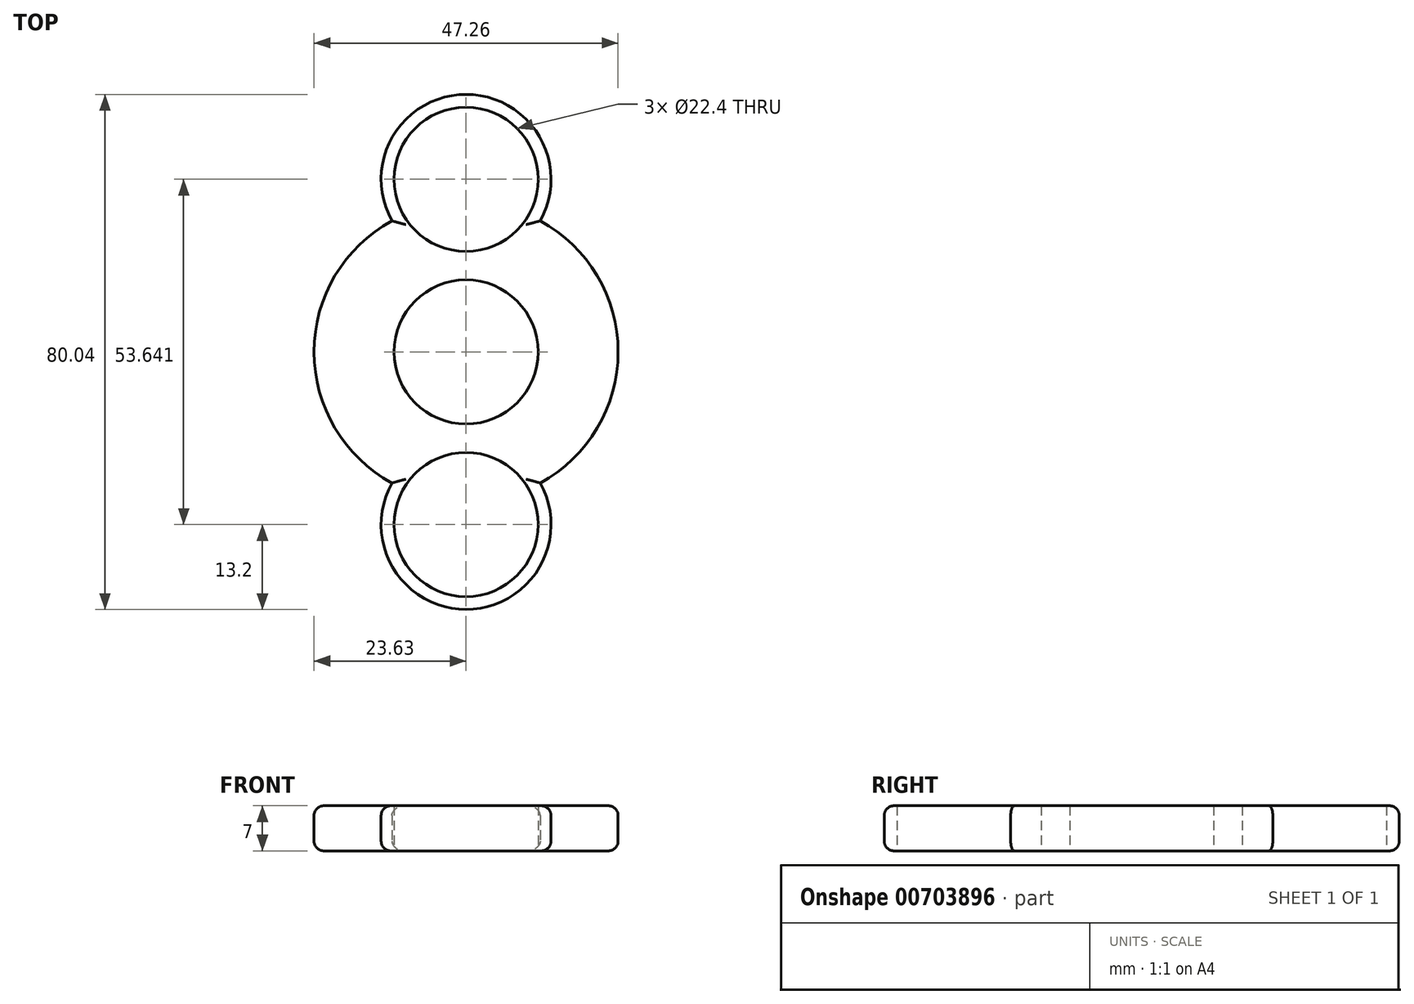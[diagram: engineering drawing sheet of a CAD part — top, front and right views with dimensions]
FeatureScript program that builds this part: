
annotation { "Feature Type Name" : "Feature", "Feature Type Description" : "" }
export const myFeature = defineFeature(function(context is Context, id is Id, definition is map)
    precondition{}
    {
        {
            var Q0;
            Q0=qCreatedBy(makeId("Top.planeOp"),FACE);
            var sketch = newSketch(context, id + "F0", { "sketchPlane" : qUnion([Q0])});
            skCircle(sketch, "E0", {"center": v(0, 0) * mm, "radius": 11.2 * mm});
            skCircle(sketch, "E1", {"center": v(0, 26.82) * mm, "radius": 11.2 * mm});
            skArc(sketch, "E2", {"start": v(11.51, 20.37) * mm, "mid": v(0, 40.02) * mm, "end": v(-11.52, 20.37) * mm});
            skCircle(sketch, "E3.1.0", {"center": v(0, -26.82) * mm, "radius": 11.2 * mm});
            skArc(sketch, "E3.1.1", {"start": v(-11.51, -20.37) * mm, "mid": v(0, -40.02) * mm, "end": v(11.52, -20.37) * mm});
            skArc(sketch, "E4", {"start": v(11.52, -20.37) * mm, "mid": v(23.63, 0) * mm, "end": v(11.51, 20.37) * mm});
            skArc(sketch, "E5.1.0", {"start": v(-11.52, 20.37) * mm, "mid": v(-23.63, 0) * mm, "end": v(-11.51, -20.37) * mm});
            skSolve(sketch);
        }
        {
            var Q0;
            Q0=makeQuery(id+"F0.imprint","IMPRINT",FACE,{"disambiguationData":[TD([[makeQuery(id+"F0.imprint","IMPRINT",EDGE,{"derivedFrom":sQuery(id+"F0.wireOp",EDGE,"E0")}),-1.0]])]});
            extrude(context, id + "F1", {"entities" : qUnion([Q0]), "depth" : 7 * mm, "offsetDistance" : 25 * mm});
        }
        {
            var Q0;
            Q0=makeQuery(id+"F1.opExtrude","CAP_EDGE",EDGE,{"disambiguationData":[OSD([sQuery(id+"F0.wireOp",EDGE,"E5.1.0")])],"isStart":false});
            var Q1;
            Q1=makeQuery(id+"F1.opExtrude","CAP_EDGE",EDGE,{"disambiguationData":[OSD([sQuery(id+"F0.wireOp",EDGE,"E2")])],"isStart":false});
            var Q2;
            Q2=makeQuery(id+"F1.opExtrude","CAP_EDGE",EDGE,{"disambiguationData":[OSD([sQuery(id+"F0.wireOp",EDGE,"E4")])],"isStart":false});
            var Q3;
            Q3=makeQuery(id+"F1.opExtrude","CAP_EDGE",EDGE,{"disambiguationData":[OSD([sQuery(id+"F0.wireOp",EDGE,"E3.1.1")])],"isStart":false});
            fillet(context, id + "F2", {"entities" : qUnion([Q0, Q1, Q2, Q3]), "radius" : 1.5 * mm, "tangentPropagation" : true, "allowEdgeOverflow" : false});
        }
        {
            var Q0;
            Q0=makeQuery(id+"F1.opExtrude","CAP_EDGE",EDGE,{"disambiguationData":[OSD([sQuery(id+"F0.wireOp",EDGE,"E4")])],"isStart":true});
            var Q1;
            Q1=makeQuery(id+"F1.opExtrude","CAP_EDGE",EDGE,{"disambiguationData":[OSD([sQuery(id+"F0.wireOp",EDGE,"E2")])],"isStart":true});
            var Q2;
            Q2=makeQuery(id+"F1.opExtrude","CAP_EDGE",EDGE,{"disambiguationData":[OSD([sQuery(id+"F0.wireOp",EDGE,"E5.1.0")])],"isStart":true});
            var Q3;
            Q3=makeQuery(id+"F1.opExtrude","CAP_EDGE",EDGE,{"disambiguationData":[OSD([sQuery(id+"F0.wireOp",EDGE,"E3.1.1")])],"isStart":true});
            fillet(context, id + "F3", {"entities" : qUnion([Q0, Q1, Q2, Q3]), "radius" : 1.5 * mm, "tangentPropagation" : true, "allowEdgeOverflow" : false});
        }
    });
